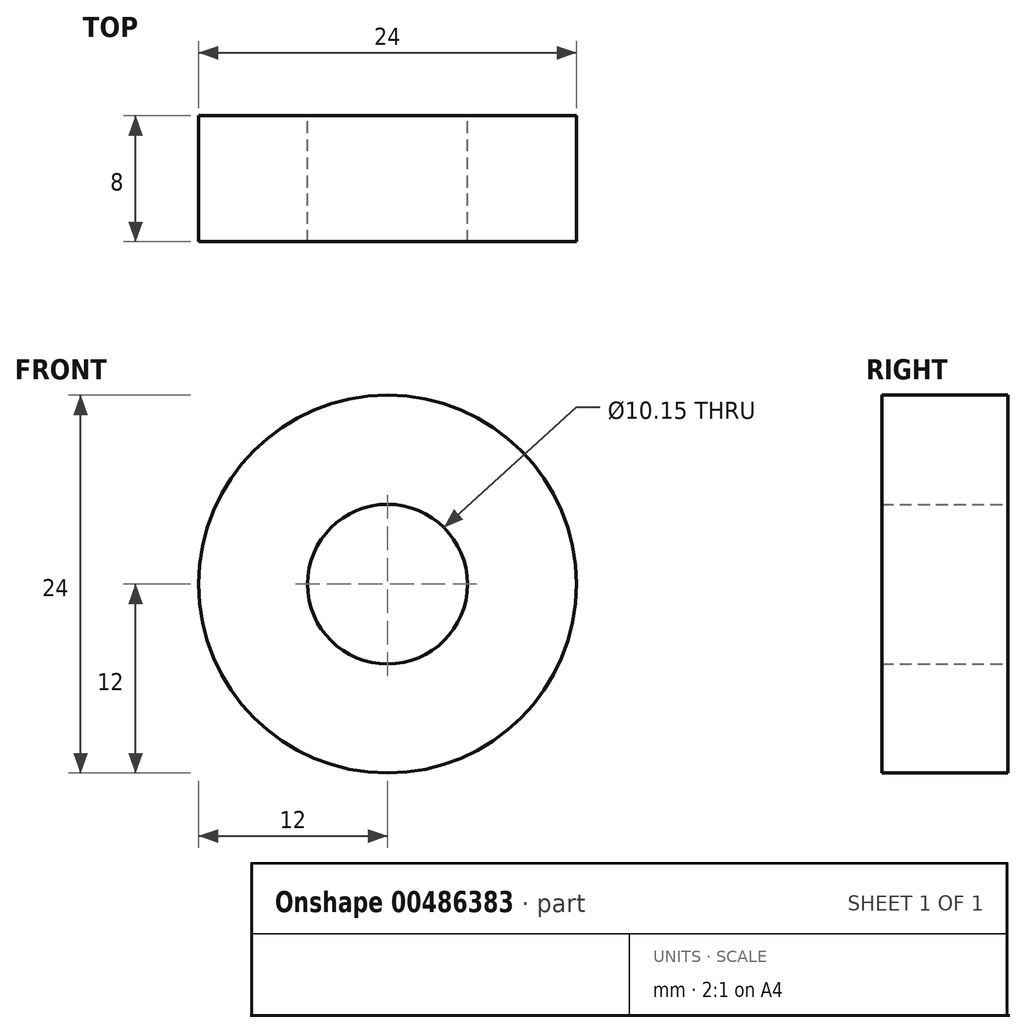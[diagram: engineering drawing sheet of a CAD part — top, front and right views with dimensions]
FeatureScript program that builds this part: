
annotation { "Feature Type Name" : "Feature", "Feature Type Description" : "" }
export const myFeature = defineFeature(function(context is Context, id is Id, definition is map)
    precondition{}
    {
        {
            var Q0;
            Q0=qCreatedBy(makeId("Front.planeOp"),FACE);
            var sketch = newSketch(context, id + "F0", { "sketchPlane" : qUnion([Q0])});
            skCircle(sketch, "E0", {"center": v(0, 0) * mm, "radius": 12 * mm});
            skCircle(sketch, "E1", {"center": v(0, 0) * mm, "radius": 5.08 * mm});
            skSolve(sketch);
        }
        {
            var Q0;
            Q0 = qSketchRegion(id + "F0", true);
            extrude(context, id + "F1", {"entities" : qUnion([Q0]), "depth" : 8 * mm});
        }
    });
